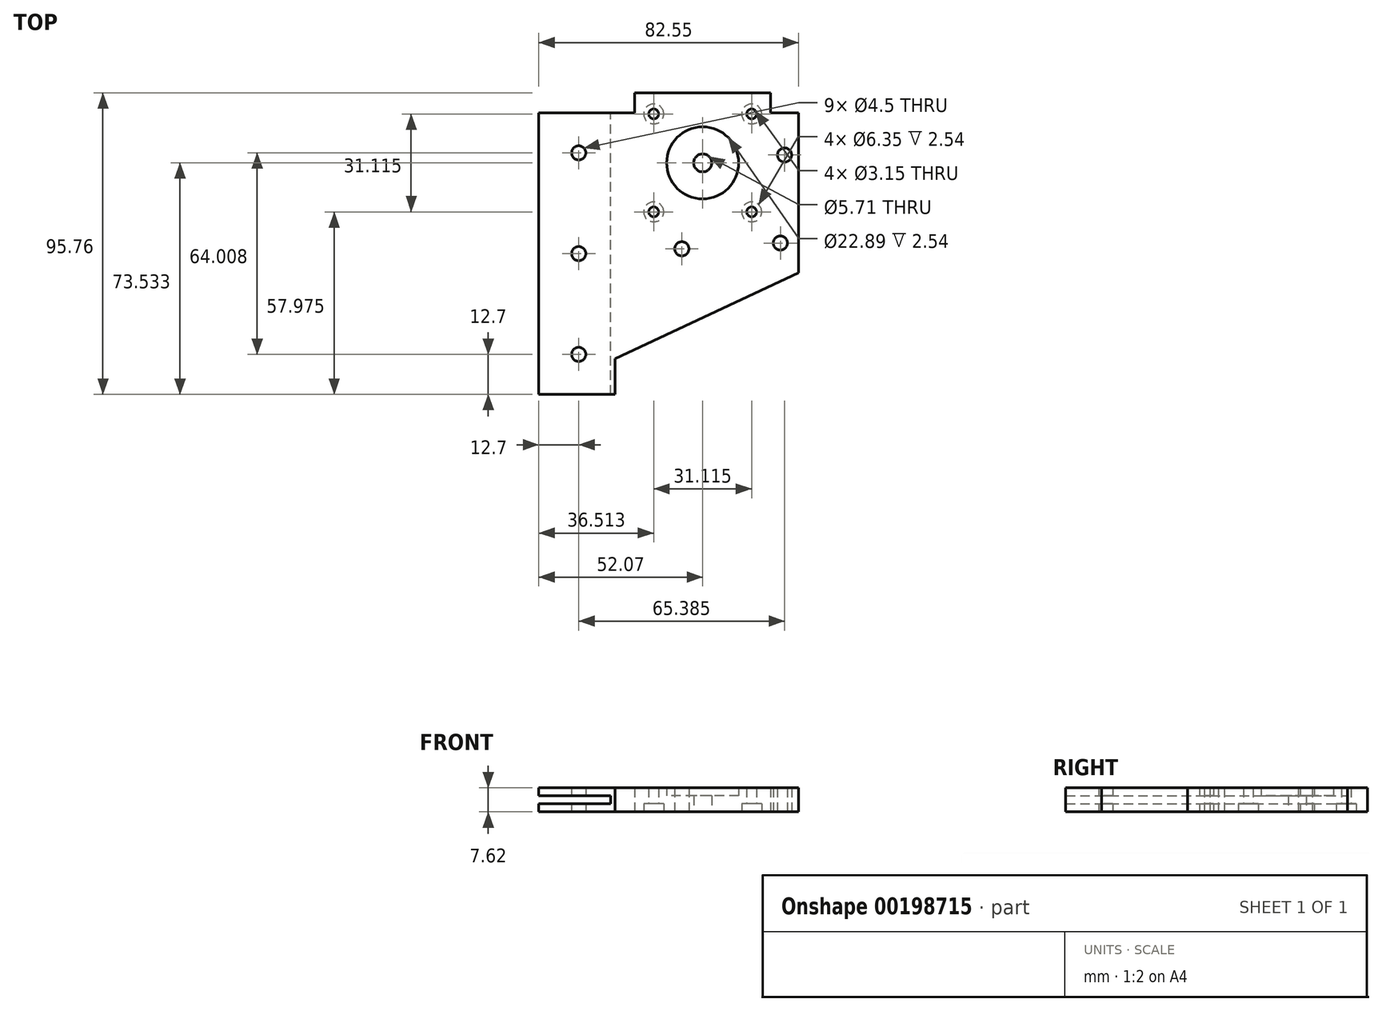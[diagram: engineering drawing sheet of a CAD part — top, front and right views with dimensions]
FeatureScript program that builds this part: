
annotation { "Feature Type Name" : "Feature", "Feature Type Description" : "" }
export const myFeature = defineFeature(function(context is Context, id is Id, definition is map)
    precondition{}
    {
        {
            var Q0;
            Q0=qCreatedBy(makeId("Top.planeOp"),FACE);
            var sketch = newSketch(context, id + "F0", { "sketchPlane" : qUnion([Q0])});
            skLineSegment(sketch, "E0", {"start": v(0, 0) * mm, "end": v(0, 89.4) * mm});
            skLineSegment(sketch, "E1", {"start": v(0, 89.4) * mm, "end": v(30.48, 89.4) * mm});
            skLineSegment(sketch, "E2", {"start": v(82.55, 89.4) * mm, "end": v(82.55, 38.6) * mm});
            skLineSegment(sketch, "E3", {"start": v(82.55, 38.6) * mm, "end": v(24.2, 11.32) * mm});
            skCircle(sketch, "E4", {"center": v(12.7, 12.7) * mm, "radius": 2.25 * mm});
            skCircle(sketch, "E5", {"center": v(12.7, 44.7) * mm, "radius": 2.25 * mm});
            skCircle(sketch, "E6", {"center": v(12.7, 76.7) * mm, "radius": 2.25 * mm});
            skLineSegment(sketch, "E7", {"start": v(0, 0) * mm, "end": v(24.2, 0) * mm});
            skLineSegment(sketch, "E8", {"start": v(24.2, 0) * mm, "end": v(24.2, 11.32) * mm});
            skCircle(sketch, "E9", {"center": v(36.51, 89.1) * mm, "radius": 3.18 * mm});
            skCircle(sketch, "E10", {"center": v(36.51, 57.98) * mm, "radius": 3.18 * mm});
            skCircle(sketch, "E11", {"center": v(67.63, 57.98) * mm, "radius": 3.18 * mm});
            skCircle(sketch, "E12", {"center": v(67.63, 89.1) * mm, "radius": 3.18 * mm});
            skCircle(sketch, "E13", {"center": v(52.07, 73.53) * mm, "radius": 2.86 * mm});
            skCircle(sketch, "E14", {"center": v(78.09, 76.04) * mm, "radius": 2.25 * mm});
            skCircle(sketch, "E15", {"center": v(45.46, 46.24) * mm, "radius": 2.25 * mm});
            skCircle(sketch, "E16", {"center": v(76.75, 48.07) * mm, "radius": 2.25 * mm});
            skLineSegment(sketch, "E17", {"start": v(30.48, 89.4) * mm, "end": v(30.48, 95.76) * mm});
            skLineSegment(sketch, "E18", {"start": v(30.48, 95.76) * mm, "end": v(73.66, 95.76) * mm});
            skLineSegment(sketch, "E19", {"start": v(73.66, 95.76) * mm, "end": v(73.66, 89.4) * mm});
            skLineSegment(sketch, "E20.trimOffspring", {"start": v(73.66, 89.4) * mm, "end": v(82.55, 89.4) * mm});
            skCircle(sketch, "E21", {"center": v(52.07, 73.53) * mm, "radius": 11.43 * mm});
            skCircle(sketch, "E22", {"center": v(36.51, 89.1) * mm, "radius": 1.46 * mm});
            skCircle(sketch, "E23", {"center": v(67.63, 89.1) * mm, "radius": 1.46 * mm});
            skCircle(sketch, "E24", {"center": v(67.63, 57.98) * mm, "radius": 1.46 * mm});
            skCircle(sketch, "E25", {"center": v(36.51, 57.98) * mm, "radius": 1.46 * mm});
            skSolve(sketch);
        }
        {
            var Q0;
            Q0=makeQuery(id+"F0.imprint","IMPRINT",FACE,{"disambiguationData":[TD([[makeQuery(id+"F0.imprint","IMPRINT",EDGE,{"derivedFrom":sQuery(id+"F0.wireOp",EDGE,"E0")}),-1.0]])]});
            var Q1;
            Q1=makeQuery(id+"F0.imprint","IMPRINT",FACE,{"disambiguationData":[TD([[makeQuery(id+"F0.imprint","IMPRINT",EDGE,{"derivedFrom":sQuery(id+"F0.wireOp",EDGE,"E13")}),-1.0]])]});
            extrude(context, id + "F1", {"entities" : qUnion([Q0, Q1]), "depth" : 2.54 * mm});
        }
        {
            var Q0;
            Q0=makeQuery(id+"F1.opExtrude","CAP_FACE",FACE,{"disambiguationData":[OSD([sQuery(id+"F0.wireOp",EDGE,"E0"),sQuery(id+"F0.wireOp",EDGE,"E1"),sQuery(id+"F0.wireOp",EDGE,"E2"),sQuery(id+"F0.wireOp",EDGE,"E3"),sQuery(id+"F0.wireOp",EDGE,"E4"),sQuery(id+"F0.wireOp",EDGE,"E5"),sQuery(id+"F0.wireOp",EDGE,"E6"),sQuery(id+"F0.wireOp",EDGE,"E7"),sQuery(id+"F0.wireOp",EDGE,"E8"),sQuery(id+"F0.wireOp",EDGE,"E9"),sQuery(id+"F0.wireOp",EDGE,"E10"),sQuery(id+"F0.wireOp",EDGE,"E11"),sQuery(id+"F0.wireOp",EDGE,"E12"),sQuery(id+"F0.wireOp",EDGE,"E13"),sQuery(id+"F0.wireOp",EDGE,"E14"),sQuery(id+"F0.wireOp",EDGE,"E15"),sQuery(id+"F0.wireOp",EDGE,"E16"),sQuery(id+"F0.wireOp",EDGE,"E17"),sQuery(id+"F0.wireOp",EDGE,"E18"),sQuery(id+"F0.wireOp",EDGE,"E19"),sQuery(id+"F0.wireOp",EDGE,"E20.trimOffspring")])],"isStart":false});
            var sketch = newSketch(context, id + "F2", { "sketchPlane" : qUnion([Q0])});
            skLineSegment(sketch, "E26", {"start": v(25.4, 89.4) * mm, "end": v(25.4, 0) * mm});
            skCircle(sketch, "E27", {"center": v(36.51, 57.98) * mm, "radius": 1.57 * mm});
            skCircle(sketch, "E28", {"center": v(36.51, 89.1) * mm, "radius": 1.57 * mm});
            skCircle(sketch, "E29", {"center": v(67.63, 57.98) * mm, "radius": 1.57 * mm});
            skCircle(sketch, "E30", {"center": v(67.63, 89.1) * mm, "radius": 1.57 * mm});
            skSolve(sketch);
        }
        {
            var Q0;
            {var subQ6=makeQuery(id+"F1.opExtrude","CAP_EDGE",EDGE,{"disambiguationData":[OSD([sQuery(id+"F0.wireOp",EDGE,"E2")])],"isStart":false});Q0=makeQuery(id+"F2.imprint","IMPRINT",FACE,{"disambiguationData":[TD([[makeQuery(id+"F2.imprint","IMPRINT",EDGE,{"derivedFrom":subQ6}),-1.0]])]});}
            var Q1;
            Q1=makeQuery(id+"F2.imprint","IMPRINT",FACE,{"disambiguationData":[TD([[makeQuery(id+"F2.imprint","IMPRINT",EDGE,{"derivedFrom":sQuery(id+"F2.wireOp",EDGE,"E27")}),-1.0]])]});
            var Q2;
            Q2=makeQuery(id+"F2.imprint","IMPRINT",FACE,{"disambiguationData":[TD([[makeQuery(id+"F2.imprint","IMPRINT",EDGE,{"derivedFrom":sQuery(id+"F2.wireOp",EDGE,"E29")}),-1.0]])]});
            var Q3;
            Q3=makeQuery(id+"F2.imprint","IMPRINT",FACE,{"disambiguationData":[TD([[makeQuery(id+"F2.imprint","IMPRINT",EDGE,{"derivedFrom":sQuery(id+"F2.wireOp",EDGE,"E30")}),-1.0]])]});
            var Q4;
            Q4=makeQuery(id+"F2.imprint","IMPRINT",FACE,{"disambiguationData":[TD([[makeQuery(id+"F2.imprint","IMPRINT",EDGE,{"derivedFrom":sQuery(id+"F2.wireOp",EDGE,"E28")}),-1.0]])]});
            extrude(context, id + "F3", {"entities" : qUnion([Q0, Q1, Q2, Q3, Q4]), "operationType" : NewBodyOperationType.ADD, "depth" : 2.54 * mm});
        }
        {
            var Q0;
            Q0=makeQuery(id+"F3.opExtrude","CAP_FACE",FACE,{"disambiguationData":[OSD([sQuery(id+"F0.wireOp",EDGE,"E1"),sQuery(id+"F0.wireOp",EDGE,"E2"),sQuery(id+"F0.wireOp",EDGE,"E3"),sQuery(id+"F0.wireOp",EDGE,"E13"),sQuery(id+"F0.wireOp",EDGE,"E14"),sQuery(id+"F0.wireOp",EDGE,"E15"),sQuery(id+"F0.wireOp",EDGE,"E16"),sQuery(id+"F0.wireOp",EDGE,"E17"),sQuery(id+"F0.wireOp",EDGE,"E18"),sQuery(id+"F0.wireOp",EDGE,"E19"),sQuery(id+"F0.wireOp",EDGE,"E20.trimOffspring"),sQuery(id+"F2.wireOp",EDGE,"E26"),sQuery(id+"F2.wireOp",EDGE,"E27"),sQuery(id+"F2.wireOp",EDGE,"E28"),sQuery(id+"F2.wireOp",EDGE,"E29"),sQuery(id+"F2.wireOp",EDGE,"E30")])],"isStart":false});
            var sketch = newSketch(context, id + "F4", { "sketchPlane" : qUnion([Q0])});
            skCircle(sketch, "E31", {"center": v(52.07, 73.53) * mm, "radius": 11.45 * mm});
            skLineSegment(sketch, "E32", {"start": v(25.4, 89.4) * mm, "end": v(0, 89.4) * mm});
            skLineSegment(sketch, "E33", {"start": v(0, 89.4) * mm, "end": v(0, 0) * mm});
            skLineSegment(sketch, "E34", {"start": v(0, 0) * mm, "end": v(25.4, 0) * mm});
            skLineSegment(sketch, "E35", {"start": v(25.4, 0) * mm, "end": v(25.4, 11.88) * mm});
            skCircle(sketch, "E36", {"center": v(12.7, 12.7) * mm, "radius": 2.25 * mm});
            skCircle(sketch, "E37", {"center": v(12.7, 44.7) * mm, "radius": 2.25 * mm});
            skCircle(sketch, "E38", {"center": v(12.7, 76.7) * mm, "radius": 2.25 * mm});
            skLineSegment(sketch, "E39", {"start": v(25.4, 11.88) * mm, "end": v(24.2, 11.31) * mm});
            skLineSegment(sketch, "E40", {"start": v(24.2, 11.31) * mm, "end": v(24.2, 0) * mm});
            skSolve(sketch);
        }
        {
            var Q0;
            Q0=makeQuery(id+"F4.imprint","IMPRINT",FACE,{"disambiguationData":[TD([[makeQuery(id+"F4.imprint","IMPRINT",EDGE,{"derivedFrom":sQuery(id+"F4.wireOp",EDGE,"E31")}),-1.0]])]});
            extrude(context, id + "F5", {"entities" : qUnion([Q0]), "operationType" : NewBodyOperationType.ADD, "depth" : 2.54 * mm});
        }
        {
            var Q0;
            Q0=makeQuery(id+"F1.opExtrude","CAP_FACE",FACE,{"disambiguationData":[OSD([sQuery(id+"F0.wireOp",EDGE,"E0"),sQuery(id+"F0.wireOp",EDGE,"E1"),sQuery(id+"F0.wireOp",EDGE,"E2"),sQuery(id+"F0.wireOp",EDGE,"E3"),sQuery(id+"F0.wireOp",EDGE,"E4"),sQuery(id+"F0.wireOp",EDGE,"E5"),sQuery(id+"F0.wireOp",EDGE,"E6"),sQuery(id+"F0.wireOp",EDGE,"E7"),sQuery(id+"F0.wireOp",EDGE,"E8"),sQuery(id+"F0.wireOp",EDGE,"E9"),sQuery(id+"F0.wireOp",EDGE,"E10"),sQuery(id+"F0.wireOp",EDGE,"E11"),sQuery(id+"F0.wireOp",EDGE,"E12"),sQuery(id+"F0.wireOp",EDGE,"E13"),sQuery(id+"F0.wireOp",EDGE,"E14"),sQuery(id+"F0.wireOp",EDGE,"E15"),sQuery(id+"F0.wireOp",EDGE,"E16"),sQuery(id+"F0.wireOp",EDGE,"E17"),sQuery(id+"F0.wireOp",EDGE,"E18"),sQuery(id+"F0.wireOp",EDGE,"E19"),sQuery(id+"F0.wireOp",EDGE,"E20.trimOffspring")])],"isStart":false});
            extrude(context, id + "F6", {"entities" : qUnion([Q0]), "operationType" : NewBodyOperationType.ADD, "depth" : 5.08 * mm});
        }
        {
            var Q0;
            {var subQ0=sQuery(id+"F0.wireOp",EDGE,"E1");Q0=makeQuery(id+"F6.boolean.opBoolean","MERGE",FACE,{"derivedFrom":[makeQuery(id+"F5.boolean.opBoolean","MERGE",FACE,{"derivedFrom":[makeQuery(id+"F3.boolean.opBoolean","MERGE",FACE,{"derivedFrom":[makeQuery(id+"F1.opExtrude","SWEPT_FACE",FACE,{"disambiguationData":[OSD([subQ0])]}),makeQuery(id+"F3.opExtrude","SWEPT_FACE",FACE,{"disambiguationData":[OSD([subQ0])]})]}),makeQuery(id+"F5.opExtrude","SWEPT_FACE",FACE,{"disambiguationData":[OSD([subQ0])]})]}),makeQuery(id+"F6.opExtrude","SWEPT_FACE",FACE,{"disambiguationData":[OSD([subQ0])]})]});}
            var sketch = newSketch(context, id + "F7", { "sketchPlane" : qUnion([Q0])});
            skLineSegment(sketch, "E41.bottom", {"start": v(0, 5.08) * mm, "end": v(-22.86, 5.08) * mm});
            skLineSegment(sketch, "E41.top", {"start": v(0, 2.54) * mm, "end": v(-22.86, 2.54) * mm});
            skLineSegment(sketch, "E41.left", {"start": v(0, 5.08) * mm, "end": v(0, 2.54) * mm});
            skLineSegment(sketch, "E41.right", {"start": v(-22.86, 5.08) * mm, "end": v(-22.86, 2.54) * mm});
            skSolve(sketch);
        }
        {
            var Q0;
            Q0=makeQuery(id+"F7.imprint","IMPRINT",FACE,{"disambiguationData":[TD([[makeQuery(id+"F7.imprint","IMPRINT",EDGE,{"derivedFrom":sQuery(id+"F7.wireOp",EDGE,"E41.bottom")}),1.0]])]});
            extrude(context, id + "F8", {"entities" : qUnion([Q0]), "operationType" : NewBodyOperationType.REMOVE, "endBound" : BoundingType.THROUGH_ALL, "oppositeDirection" : true, "depth" : 25.4 * mm});
        }
    });
